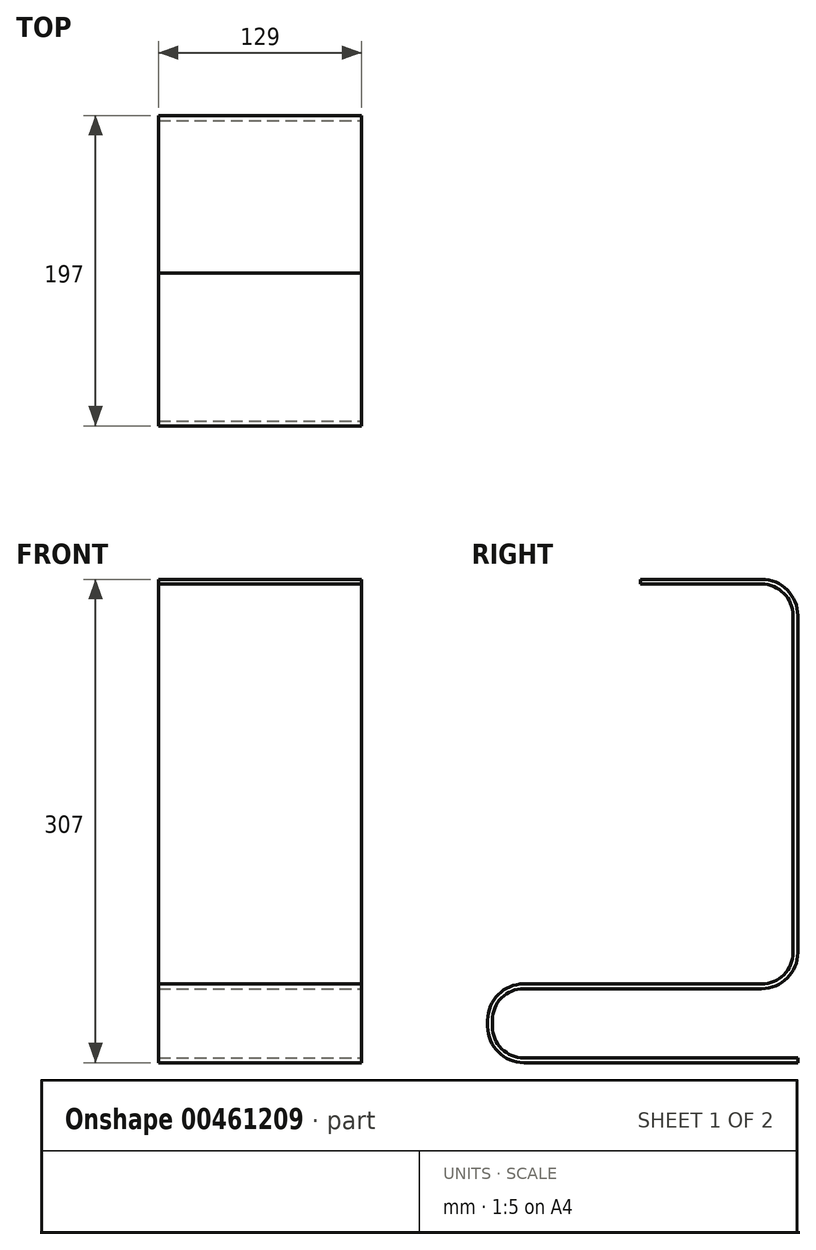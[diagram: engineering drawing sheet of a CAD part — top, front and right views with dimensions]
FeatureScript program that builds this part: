
annotation { "Feature Type Name" : "Feature", "Feature Type Description" : "" }
export const myFeature = defineFeature(function(context is Context, id is Id, definition is map)
    precondition{}
    {
        {
            var Q0;
            Q0=qCreatedBy(makeId("Right.planeOp"),FACE);
            var sketch = newSketch(context, id + "F0", { "sketchPlane" : qUnion([Q0])});
            skLineSegment(sketch, "E0.bottom", {"start": v(74, 47) * mm, "end": v(-77, 47) * mm});
            skLineSegment(sketch, "E0.top", {"start": v(97, 3) * mm, "end": v(-77, 3) * mm});
            skLineSegment(sketch, "E0.left", {"start": v(97, 47) * mm, "end": v(97, 3) * mm});
            skLineSegment(sketch, "E0.right", {"start": v(-97, 27) * mm, "end": v(-97, 23) * mm});
            skPoint(sketch, "E0.middle", {"position": v(0, 25) * mm});
            skPoint(sketch, "E1.visualSharp", {"position": v(-97, 47) * mm});
            skArc(sketch, "E1.filletArc", {"start": v(-77, 47) * mm, "mid": v(-91.14, 41.14) * mm, "end": v(-97, 27) * mm});
            skPoint(sketch, "E2.visualSharp", {"position": v(-97, 3) * mm});
            skArc(sketch, "E2.filletArc", {"start": v(-97, 23) * mm, "mid": v(-91.14, 8.86) * mm, "end": v(-77, 3) * mm});
            skLineSegment(sketch, "E3", {"start": v(97, 3) * mm, "end": v(97, 0) * mm});
            skLineSegment(sketch, "E4", {"start": v(97, 0) * mm, "end": v(-77, 0) * mm});
            skLineSegment(sketch, "E5", {"start": v(97, 47) * mm, "end": v(97, 50) * mm});
            skLineSegment(sketch, "E6", {"start": v(74, 50) * mm, "end": v(-77, 50) * mm});
            skLineSegment(sketch, "E7", {"start": v(-100, 27) * mm, "end": v(-100, 23) * mm});
            skPoint(sketch, "E8.visualSharp", {"position": v(-100, 50) * mm});
            skArc(sketch, "E8.filletArc", {"start": v(-77, 50) * mm, "mid": v(-93.26, 43.26) * mm, "end": v(-100, 27) * mm});
            skPoint(sketch, "E9.visualSharp", {"position": v(-100, 0) * mm});
            skArc(sketch, "E9.filletArc", {"start": v(-100, 23) * mm, "mid": v(-93.26, 6.74) * mm, "end": v(-77, 0) * mm});
            skLineSegment(sketch, "E10", {"start": v(97, 70) * mm, "end": v(97, 287) * mm});
            skLineSegment(sketch, "E11", {"start": v(77, 307) * mm, "end": v(-3, 307) * mm});
            skLineSegment(sketch, "E12", {"start": v(-3, 307) * mm, "end": v(-3, 304) * mm});
            skLineSegment(sketch, "E13", {"start": v(-3, 304) * mm, "end": v(74, 304) * mm});
            skLineSegment(sketch, "E14", {"start": v(94, 284) * mm, "end": v(94, 70) * mm});
            skPoint(sketch, "E15.visualSharp", {"position": v(94, 304) * mm});
            skArc(sketch, "E15.filletArc", {"start": v(94, 284) * mm, "mid": v(88.14, 298.14) * mm, "end": v(74, 304) * mm});
            skPoint(sketch, "E16.visualSharp", {"position": v(97, 307) * mm});
            skPoint(sketch, "E17.newPointA", {"position": v(97, 50) * mm});
            skArc(sketch, "E17.filletArc", {"start": v(74, 50) * mm, "mid": v(88.14, 55.86) * mm, "end": v(94, 70) * mm});
            skPoint(sketch, "E18.visualSharp", {"position": v(97, 47) * mm});
            skArc(sketch, "E18.filletArc", {"start": v(74, 47) * mm, "mid": v(90.26, 53.74) * mm, "end": v(97, 70) * mm});
            skLineSegment(sketch, "E19", {"start": v(74, 307) * mm, "end": v(77, 307) * mm});
            skLineSegment(sketch, "E20", {"start": v(97, 284) * mm, "end": v(97, 287) * mm});
            skArc(sketch, "E21.filletArc", {"start": v(97, 284) * mm, "mid": v(90.26, 300.26) * mm, "end": v(74, 307) * mm});
            skSolve(sketch);
        }
        {
            var Q0;
            Q0=makeQuery(id+"F0.imprint","IMPRINT",FACE,{"disambiguationData":[TD([[makeQuery(id+"F0.imprint","IMPRINT",EDGE,{"derivedFrom":sQuery(id+"F0.wireOp",EDGE,"E0.bottom")}),-1.0]])]});
            extrude(context, id + "F1", {"entities" : qUnion([Q0]), "endBound" : BoundingType.SYMMETRIC, "oppositeDirection" : true, "depth" : 129 * mm, "offsetDistance" : 25 * mm});
        }
    });
